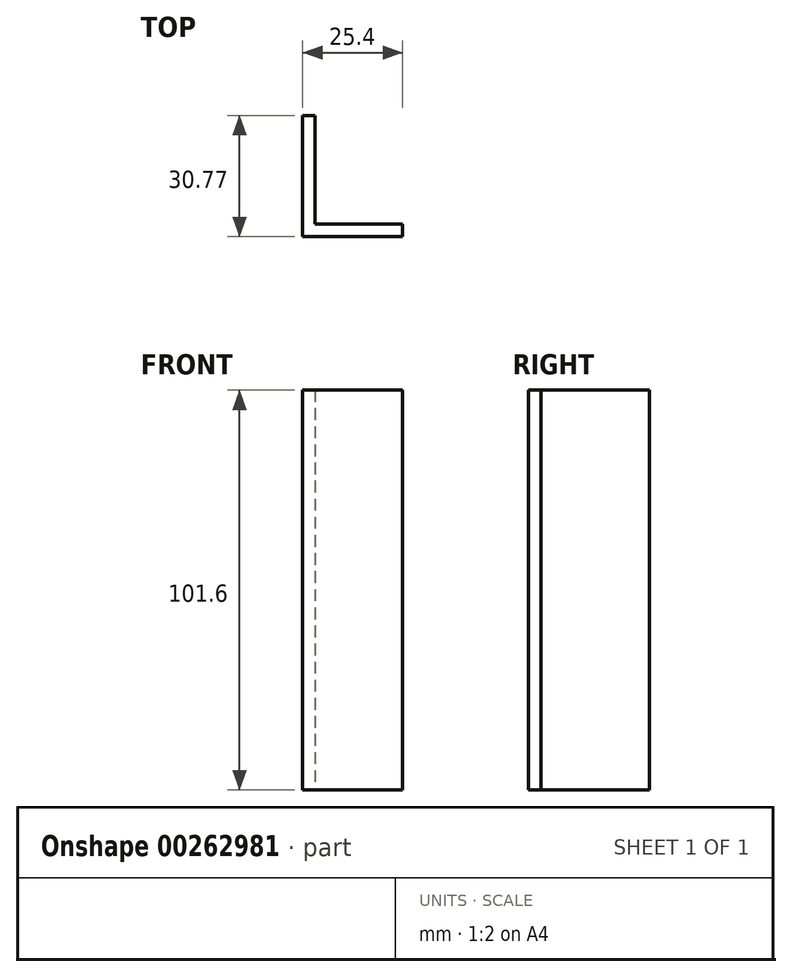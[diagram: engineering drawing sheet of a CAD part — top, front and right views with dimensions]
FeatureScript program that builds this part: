
annotation { "Feature Type Name" : "Feature", "Feature Type Description" : "" }
export const myFeature = defineFeature(function(context is Context, id is Id, definition is map)
    precondition{}
    {
        {
            var Q0;
            Q0=qCreatedBy(makeId("Top.planeOp"),FACE);
            var sketch = newSketch(context, id + "F0", { "sketchPlane" : qUnion([Q0])});
            skLineSegment(sketch, "E0", {"start": v(0, 30.77) * mm, "end": v(0, 0) * mm});
            skLineSegment(sketch, "E1", {"start": v(0, 0) * mm, "end": v(25.4, 0) * mm});
            skLineSegment(sketch, "E2", {"start": v(25.4, 0) * mm, "end": v(25.4, 3.18) * mm});
            skLineSegment(sketch, "E3", {"start": v(25.4, 3.18) * mm, "end": v(3.18, 3.18) * mm});
            skLineSegment(sketch, "E4", {"start": v(3.18, 3.18) * mm, "end": v(3.18, 30.77) * mm});
            skLineSegment(sketch, "E5", {"start": v(3.18, 30.77) * mm, "end": v(0, 30.77) * mm});
            skSolve(sketch);
        }
        {
            var Q0;
            Q0=makeQuery(id+"F0.imprint","IMPRINT",FACE,{"disambiguationData":[TD([[makeQuery(id+"F0.imprint","IMPRINT",EDGE,{"derivedFrom":sQuery(id+"F0.wireOp",EDGE,"E0")}),1.0]])]});
            extrude(context, id + "F1", {"entities" : qUnion([Q0]), "depth" : 101.6 * mm});
        }
    });
